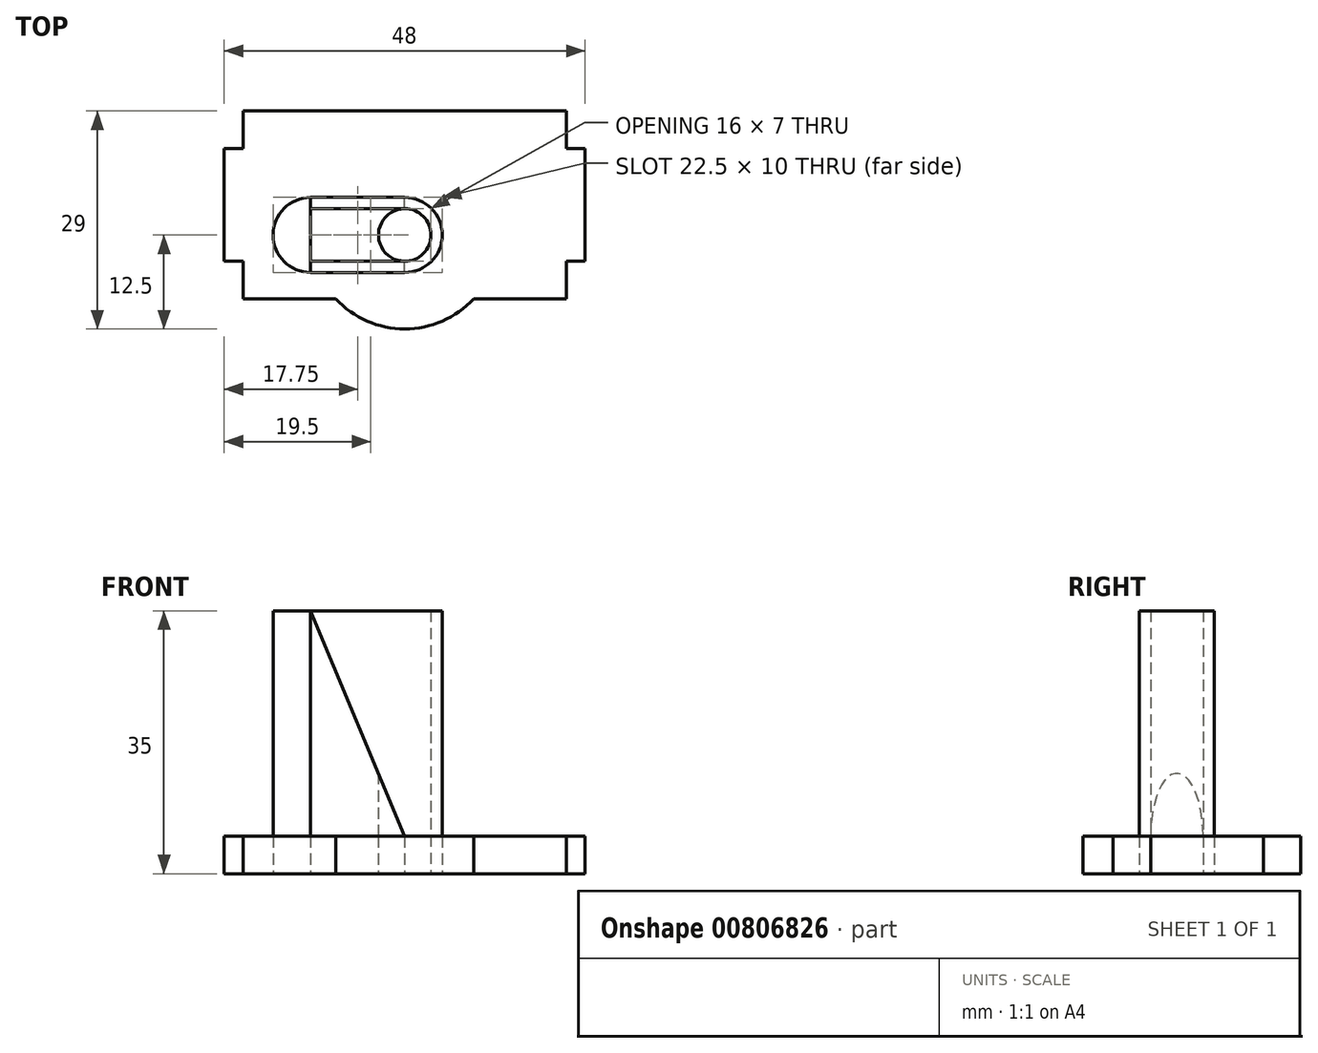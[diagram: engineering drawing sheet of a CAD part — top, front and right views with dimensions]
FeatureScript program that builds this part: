
annotation { "Feature Type Name" : "Feature", "Feature Type Description" : "" }
export const myFeature = defineFeature(function(context is Context, id is Id, definition is map)
    precondition{}
    {
        {
            var Q0;
            Q0=qCreatedBy(makeId("Top.planeOp"),FACE);
            var sketch = newSketch(context, id + "F0", { "sketchPlane" : qUnion([Q0])});
            skCircle(sketch, "E0", {"center": v(0, 0) * mm, "radius": 12.5 * mm});
            skCircle(sketch, "E1", {"center": v(0, 0) * mm, "radius": 3.5 * mm});
            skCircle(sketch, "E2", {"center": v(-12.5, 0) * mm, "radius": 5 * mm});
            skCircle(sketch, "E3", {"center": v(-12.5, 0) * mm, "radius": 3 * mm});
            skCircle(sketch, "E4", {"center": v(0, 0) * mm, "radius": 5 * mm});
            skLineSegment(sketch, "E5.bottom", {"start": v(0, 3.5) * mm, "end": v(-12.5, 3.5) * mm});
            skLineSegment(sketch, "E5.top", {"start": v(0, 5) * mm, "end": v(-12.5, 5) * mm});
            skLineSegment(sketch, "E5.left", {"start": v(0, 3.5) * mm, "end": v(0, 5) * mm});
            skLineSegment(sketch, "E5.right", {"start": v(-12.5, 3.5) * mm, "end": v(-12.5, 5) * mm});
            skLineSegment(sketch, "E6.bottom", {"start": v(0, -3.5) * mm, "end": v(-12.5, -3.5) * mm});
            skLineSegment(sketch, "E6.top", {"start": v(0, -5) * mm, "end": v(-12.5, -5) * mm});
            skLineSegment(sketch, "E6.left", {"start": v(0, -3.5) * mm, "end": v(0, -5) * mm});
            skLineSegment(sketch, "E6.right", {"start": v(-12.5, -3.5) * mm, "end": v(-12.5, -5) * mm});
            skLineSegment(sketch, "E7.bottom", {"start": v(12.5, 5) * mm, "end": v(-12.5, 5) * mm});
            skLineSegment(sketch, "E7.top", {"start": v(12.5, -5) * mm, "end": v(-12.5, -5) * mm});
            skLineSegment(sketch, "E7.right", {"start": v(-12.5, 5) * mm, "end": v(-12.5, -5) * mm});
            skLineSegment(sketch, "E8.bottom", {"start": v(0, 0) * mm, "end": v(24, 0) * mm});
            skLineSegment(sketch, "E8.top", {"start": v(0, -8.5) * mm, "end": v(24, -8.5) * mm});
            skLineSegment(sketch, "E8.left", {"start": v(0, 0) * mm, "end": v(0, -8.5) * mm});
            skLineSegment(sketch, "E8.right", {"start": v(24, 0) * mm, "end": v(24, -8.5) * mm});
            skLineSegment(sketch, "E9.bottom", {"start": v(0, 0) * mm, "end": v(-24, 0) * mm});
            skLineSegment(sketch, "E9.top", {"start": v(0, -8.5) * mm, "end": v(-24, -8.5) * mm});
            skLineSegment(sketch, "E9.right", {"start": v(-24, 0) * mm, "end": v(-24, -8.5) * mm});
            skLineSegment(sketch, "E10.top", {"start": v(0, 16.5) * mm, "end": v(24, 16.5) * mm});
            skLineSegment(sketch, "E10.left", {"start": v(0, 0) * mm, "end": v(0, 16.5) * mm});
            skLineSegment(sketch, "E10.right", {"start": v(24, 0) * mm, "end": v(24, 16.5) * mm});
            skLineSegment(sketch, "E11.top", {"start": v(0, 16.5) * mm, "end": v(-24, 16.5) * mm});
            skLineSegment(sketch, "E11.right", {"start": v(-24, 0) * mm, "end": v(-24, 16.5) * mm});
            skLineSegment(sketch, "E12.bottom", {"start": v(-24, -8.5) * mm, "end": v(-21.5, -8.5) * mm});
            skLineSegment(sketch, "E12.top", {"start": v(-24, -3.5) * mm, "end": v(-21.5, -3.5) * mm});
            skLineSegment(sketch, "E12.left", {"start": v(-24, -8.5) * mm, "end": v(-24, -3.5) * mm});
            skLineSegment(sketch, "E12.right", {"start": v(-21.5, -8.5) * mm, "end": v(-21.5, -3.5) * mm});
            skLineSegment(sketch, "E13.bottom", {"start": v(-24, 16.5) * mm, "end": v(-21.5, 16.5) * mm});
            skLineSegment(sketch, "E13.top", {"start": v(-24, 11.5) * mm, "end": v(-21.5, 11.5) * mm});
            skLineSegment(sketch, "E13.left", {"start": v(-24, 16.5) * mm, "end": v(-24, 11.5) * mm});
            skLineSegment(sketch, "E13.right", {"start": v(-21.5, 16.5) * mm, "end": v(-21.5, 11.5) * mm});
            skLineSegment(sketch, "E14.bottom", {"start": v(24, 16.5) * mm, "end": v(21.5, 16.5) * mm});
            skLineSegment(sketch, "E14.top", {"start": v(24, 11.5) * mm, "end": v(21.5, 11.5) * mm});
            skLineSegment(sketch, "E14.left", {"start": v(24, 16.5) * mm, "end": v(24, 11.5) * mm});
            skLineSegment(sketch, "E14.right", {"start": v(21.5, 16.5) * mm, "end": v(21.5, 11.5) * mm});
            skPoint(sketch, "E15.oppositeSnap0", {"position": v(-6.25, -3.5) * mm});
            skLineSegment(sketch, "E15.bottom", {"start": v(24, -8.5) * mm, "end": v(21.5, -8.5) * mm});
            skLineSegment(sketch, "E15.top", {"start": v(24, -3.5) * mm, "end": v(21.5, -3.5) * mm});
            skLineSegment(sketch, "E15.left", {"start": v(24, -8.5) * mm, "end": v(24, -3.5) * mm});
            skLineSegment(sketch, "E15.right", {"start": v(21.5, -8.5) * mm, "end": v(21.5, -3.5) * mm});
            skSolve(sketch);
        }
        {
            var Q0;
            Q0=qCreatedBy(makeId("Front.planeOp"),FACE);
            var sketch = newSketch(context, id + "F1", { "sketchPlane" : qUnion([Q0])});
            skLineSegment(sketch, "E16", {"start": v(0, 0) * mm, "end": v(0, 10) * mm});
            skLineSegment(sketch, "E17", {"start": v(0, 10) * mm, "end": v(-12.5, 10) * mm});
            skLineSegment(sketch, "E18", {"start": v(-12.5, 10) * mm, "end": v(-12.5, 40) * mm});
            skLineSegment(sketch, "E19", {"start": v(-12.5, 40) * mm, "end": v(0, 10) * mm});
            skSolve(sketch);
        }
        {
            var Q0;
            Q0=makeQuery(id+"F1.imprint","IMPRINT",FACE,{"disambiguationData":[TD([[makeQuery(id+"F1.imprint","IMPRINT",EDGE,{"derivedFrom":sQuery(id+"F1.wireOp",EDGE,"E17")}),-1.0]])]});
            extrude(context, id + "F2", {"entities" : qUnion([Q0]), "endBound" : BoundingType.SYMMETRIC, "depth" : 10 * mm, "offsetDistance" : 25 * mm});
        }
        {
            var Q0;
            {var subQ1=sQuery(id+"F0.wireOp",EDGE,"E5.left");Q0=makeQuery(id+"F0.imprint","IMPRINT",FACE,{"disambiguationData":[TD([[makeQuery(id+"F0.imprint","IMPRINT",EDGE,{"derivedFrom":subQ1}),-1.0]])]});}
            var Q1;
            {var subQ1=sQuery(id+"F0.wireOp",EDGE,"E6.left");Q1=makeQuery(id+"F0.imprint","IMPRINT",FACE,{"disambiguationData":[TD([[makeQuery(id+"F0.imprint","IMPRINT",EDGE,{"derivedFrom":subQ1}),1.0]])]});}
            var Q2;
            {var subQ3=sQuery(id+"F0.wireOp",EDGE,"E2");var subQ5=sQuery(id+"F0.wireOp",EDGE,"E0");var subQ6=makeQuery(id+"F0.imprint","INTERSECT",VERTEX,{"disambiguationData":[OD(1.0)],"derivedFrom":[subQ5,subQ3]});Q2=makeQuery(id+"F0.imprint","IMPRINT",FACE,{"disambiguationData":[TD([[makeQuery(id+"F0.imprint","IMPRINT",EDGE,{"disambiguationData":[TD([[subQ6,-1.0]])],"derivedFrom":subQ5}),1.0]])]});}
            var Q3;
            {var subQ5=sQuery(id+"F0.wireOp",EDGE,"E5.top");var subQ7=sQuery(id+"F0.wireOp",EDGE,"E0");var subQ9=makeQuery(id+"F0.imprint","INTERSECT",VERTEX,{"derivedFrom":[subQ7,subQ5]});Q3=makeQuery(id+"F0.imprint","IMPRINT",FACE,{"disambiguationData":[TD([[makeQuery(id+"F0.imprint","IMPRINT",EDGE,{"disambiguationData":[TD([[subQ9,-1.0]])],"derivedFrom":subQ7}),1.0]])]});}
            var Q4;
            {var subQ4=sQuery(id+"F0.wireOp",EDGE,"E5.left");Q4=makeQuery(id+"F0.imprint","IMPRINT",FACE,{"disambiguationData":[TD([[makeQuery(id+"F0.imprint","IMPRINT",EDGE,{"derivedFrom":subQ4}),1.0]])]});}
            var Q5;
            {var subQ4=sQuery(id+"F0.wireOp",EDGE,"E6.left");Q5=makeQuery(id+"F0.imprint","IMPRINT",FACE,{"disambiguationData":[TD([[makeQuery(id+"F0.imprint","IMPRINT",EDGE,{"derivedFrom":subQ4}),-1.0]])]});}
            var Q6;
            {var subQ1=sQuery(id+"F0.wireOp",EDGE,"E5.right");Q6=makeQuery(id+"F0.imprint","IMPRINT",FACE,{"disambiguationData":[TD([[makeQuery(id+"F0.imprint","IMPRINT",EDGE,{"derivedFrom":subQ1}),1.0]])]});}
            var Q7;
            {var subQ1=sQuery(id+"F0.wireOp",EDGE,"E6.right");Q7=makeQuery(id+"F0.imprint","IMPRINT",FACE,{"disambiguationData":[TD([[makeQuery(id+"F0.imprint","IMPRINT",EDGE,{"derivedFrom":subQ1}),-1.0]])]});}
            var Q8;
            {var subQ0=sQuery(id+"F0.wireOp",EDGE,"E9.bottom");var subQ1=sQuery(id+"F0.wireOp",EDGE,"E3");var subQ2=makeQuery(id+"F0.imprint","INTERSECT",VERTEX,{"disambiguationData":[OD(1.0)],"derivedFrom":[subQ1,subQ0]});Q8=makeQuery(id+"F0.imprint","IMPRINT",FACE,{"disambiguationData":[TD([[makeQuery(id+"F0.imprint","IMPRINT",EDGE,{"disambiguationData":[TD([[subQ2,-1.0]])],"derivedFrom":subQ1}),1.0]])]});}
            var Q9;
            {var subQ0=sQuery(id+"F0.wireOp",EDGE,"E7.right");var subQ1=sQuery(id+"F0.wireOp",EDGE,"E3");var subQ2=makeQuery(id+"F0.imprint","INTERSECT",VERTEX,{"disambiguationData":[OD(0.0)],"derivedFrom":[subQ1,subQ0]});Q9=makeQuery(id+"F0.imprint","IMPRINT",FACE,{"disambiguationData":[TD([[makeQuery(id+"F0.imprint","IMPRINT",EDGE,{"disambiguationData":[TD([[subQ2,-1.0]])],"derivedFrom":subQ1}),1.0]])]});}
            var Q10;
            {var subQ5=sQuery(id+"F0.wireOp",EDGE,"E5.right");Q10=makeQuery(id+"F0.imprint","IMPRINT",FACE,{"disambiguationData":[TD([[makeQuery(id+"F0.imprint","IMPRINT",EDGE,{"derivedFrom":subQ5}),-1.0]])]});}
            var Q11;
            {var subQ5=sQuery(id+"F0.wireOp",EDGE,"E6.right");Q11=makeQuery(id+"F0.imprint","IMPRINT",FACE,{"disambiguationData":[TD([[makeQuery(id+"F0.imprint","IMPRINT",EDGE,{"derivedFrom":subQ5}),1.0]])]});}
            var Q12;
            {var subQ0=sQuery(id+"F0.wireOp",EDGE,"E2");var subQ1=sQuery(id+"F0.wireOp",EDGE,"E0");var subQ2=makeQuery(id+"F0.imprint","INTERSECT",VERTEX,{"disambiguationData":[OD(0.0)],"derivedFrom":[subQ1,subQ0]});Q12=makeQuery(id+"F0.imprint","IMPRINT",FACE,{"disambiguationData":[TD([[makeQuery(id+"F0.imprint","IMPRINT",EDGE,{"disambiguationData":[TD([[subQ2,-1.0]])],"derivedFrom":subQ1}),1.0]])]});}
            var Q13;
            {var subQ0=sQuery(id+"F0.wireOp",EDGE,"E6.bottom");var subQ1=sQuery(id+"F0.wireOp",EDGE,"E0");var subQ2=makeQuery(id+"F0.imprint","INTERSECT",VERTEX,{"derivedFrom":[subQ1,subQ0]});Q13=makeQuery(id+"F0.imprint","IMPRINT",FACE,{"disambiguationData":[TD([[makeQuery(id+"F0.imprint","IMPRINT",EDGE,{"disambiguationData":[TD([[subQ2,-1.0]])],"derivedFrom":subQ1}),1.0]])]});}
            var Q14;
            {var subQ0=sQuery(id+"F0.wireOp",EDGE,"E5.top");var subQ1=sQuery(id+"F0.wireOp",EDGE,"E0");var subQ2=makeQuery(id+"F0.imprint","INTERSECT",VERTEX,{"derivedFrom":[subQ1,subQ0]});Q14=makeQuery(id+"F0.imprint","IMPRINT",FACE,{"disambiguationData":[TD([[makeQuery(id+"F0.imprint","IMPRINT",EDGE,{"disambiguationData":[TD([[subQ2,-1.0]])],"derivedFrom":subQ1}),-1.0]])]});}
            var Q15;
            {var subQ0=sQuery(id+"F0.wireOp",EDGE,"E2");var subQ1=sQuery(id+"F0.wireOp",EDGE,"E0");var subQ2=makeQuery(id+"F0.imprint","INTERSECT",VERTEX,{"disambiguationData":[OD(1.0)],"derivedFrom":[subQ1,subQ0]});Q15=makeQuery(id+"F0.imprint","IMPRINT",FACE,{"disambiguationData":[TD([[makeQuery(id+"F0.imprint","IMPRINT",EDGE,{"disambiguationData":[TD([[subQ2,-1.0]])],"derivedFrom":subQ1}),-1.0]])]});}
            extrude(context, id + "F3", {"entities" : qUnion([Q0, Q1, Q2, Q3, Q4, Q5, Q6, Q7, Q8, Q9, Q10, Q11, Q12, Q13, Q14, Q15]), "depth" : 40 * mm, "offsetDistance" : 25 * mm});
        }
        {
            var Q0;
            {var subQ14=sQuery(id+"F0.wireOp",EDGE,"E13.top");Q0=makeQuery(id+"F0.imprint","IMPRINT",FACE,{"disambiguationData":[TD([[makeQuery(id+"F0.imprint","IMPRINT",EDGE,{"derivedFrom":subQ14}),-1.0]])]});}
            var Q1;
            {var subQ9=sQuery(id+"F0.wireOp",EDGE,"E12.top");Q1=makeQuery(id+"F0.imprint","IMPRINT",FACE,{"disambiguationData":[TD([[makeQuery(id+"F0.imprint","IMPRINT",EDGE,{"derivedFrom":subQ9}),1.0]])]});}
            var Q2;
            {var subQ0=sQuery(id+"F0.wireOp",EDGE,"E9.top");var subQ1=sQuery(id+"F0.wireOp",EDGE,"E0");var subQ2=makeQuery(id+"F0.imprint","INTERSECT",VERTEX,{"derivedFrom":[subQ1,subQ0]});Q2=makeQuery(id+"F0.imprint","IMPRINT",FACE,{"disambiguationData":[TD([[makeQuery(id+"F0.imprint","IMPRINT",EDGE,{"disambiguationData":[TD([[subQ2,1.0]])],"derivedFrom":subQ1}),1.0]])]});}
            var Q3;
            {var subQ0=sQuery(id+"F0.wireOp",EDGE,"E7.top");var subQ1=sQuery(id+"F0.wireOp",EDGE,"E0");var subQ2=makeQuery(id+"F0.imprint","INTERSECT",VERTEX,{"derivedFrom":[subQ1,subQ0]});Q3=makeQuery(id+"F0.imprint","IMPRINT",FACE,{"disambiguationData":[TD([[makeQuery(id+"F0.imprint","IMPRINT",EDGE,{"disambiguationData":[TD([[subQ2,1.0]])],"derivedFrom":subQ1}),1.0]])]});}
            var Q4;
            {var subQ0=sQuery(id+"F0.wireOp",EDGE,"E8.top");var subQ1=sQuery(id+"F0.wireOp",EDGE,"E0");var subQ2=makeQuery(id+"F0.imprint","INTERSECT",VERTEX,{"derivedFrom":[subQ1,subQ0]});Q4=makeQuery(id+"F0.imprint","IMPRINT",FACE,{"disambiguationData":[TD([[makeQuery(id+"F0.imprint","IMPRINT",EDGE,{"disambiguationData":[TD([[subQ2,1.0]])],"derivedFrom":subQ1}),1.0]])]});}
            var Q5;
            {var subQ9=sQuery(id+"F0.wireOp",EDGE,"E15.top");Q5=makeQuery(id+"F0.imprint","IMPRINT",FACE,{"disambiguationData":[TD([[makeQuery(id+"F0.imprint","IMPRINT",EDGE,{"derivedFrom":subQ9}),-1.0]])]});}
            var Q6;
            {var subQ8=sQuery(id+"F0.wireOp",EDGE,"E14.top");Q6=makeQuery(id+"F0.imprint","IMPRINT",FACE,{"disambiguationData":[TD([[makeQuery(id+"F0.imprint","IMPRINT",EDGE,{"derivedFrom":subQ8}),1.0]])]});}
            var Q7;
            {var subQ0=sQuery(id+"F0.wireOp",EDGE,"E7.bottom");var subQ1=sQuery(id+"F0.wireOp",EDGE,"E0");var subQ2=makeQuery(id+"F0.imprint","INTERSECT",VERTEX,{"derivedFrom":[subQ1,subQ0]});Q7=makeQuery(id+"F0.imprint","IMPRINT",FACE,{"disambiguationData":[TD([[makeQuery(id+"F0.imprint","IMPRINT",EDGE,{"disambiguationData":[TD([[subQ2,-1.0]])],"derivedFrom":subQ1}),1.0]])]});}
            var Q8;
            {var subQ0=sQuery(id+"F0.wireOp",EDGE,"E10.left");var subQ1=sQuery(id+"F0.wireOp",EDGE,"E0");var subQ2=makeQuery(id+"F0.imprint","INTERSECT",VERTEX,{"derivedFrom":[subQ1,subQ0]});Q8=makeQuery(id+"F0.imprint","IMPRINT",FACE,{"disambiguationData":[TD([[makeQuery(id+"F0.imprint","IMPRINT",EDGE,{"disambiguationData":[TD([[subQ2,-1.0]])],"derivedFrom":subQ1}),1.0]])]});}
            var Q9;
            {var subQ0=sQuery(id+"F0.wireOp",EDGE,"E5.bottom");var subQ5=sQuery(id+"F0.wireOp",EDGE,"E4");var subQ6=makeQuery(id+"F0.imprint","INTERSECT",VERTEX,{"derivedFrom":[subQ5,subQ0]});Q9=makeQuery(id+"F0.imprint","IMPRINT",FACE,{"disambiguationData":[TD([[makeQuery(id+"F0.imprint","IMPRINT",EDGE,{"disambiguationData":[TD([[subQ6,-1.0]])],"derivedFrom":subQ5}),1.0]])]});}
            var Q10;
            {var subQ0=sQuery(id+"F0.wireOp",EDGE,"E5.bottom");var subQ1=sQuery(id+"F0.wireOp",EDGE,"E2");var subQ2=makeQuery(id+"F0.imprint","INTERSECT",VERTEX,{"derivedFrom":[subQ1,subQ0]});Q10=makeQuery(id+"F0.imprint","IMPRINT",FACE,{"disambiguationData":[TD([[makeQuery(id+"F0.imprint","IMPRINT",EDGE,{"disambiguationData":[TD([[subQ2,1.0]])],"derivedFrom":subQ1}),-1.0]])]});}
            var Q11;
            {var subQ0=sQuery(id+"F0.wireOp",EDGE,"E9.bottom");var subQ1=sQuery(id+"F0.wireOp",EDGE,"E2");var subQ2=makeQuery(id+"F0.imprint","INTERSECT",VERTEX,{"disambiguationData":[OD(1.0)],"derivedFrom":[subQ1,subQ0]});Q11=makeQuery(id+"F0.imprint","IMPRINT",FACE,{"disambiguationData":[TD([[makeQuery(id+"F0.imprint","IMPRINT",EDGE,{"disambiguationData":[TD([[subQ2,1.0]])],"derivedFrom":subQ1}),-1.0]])]});}
            var Q12;
            {var subQ0=sQuery(id+"F0.wireOp",EDGE,"E6.bottom");var subQ5=sQuery(id+"F0.wireOp",EDGE,"E4");var subQ6=makeQuery(id+"F0.imprint","INTERSECT",VERTEX,{"derivedFrom":[subQ5,subQ0]});Q12=makeQuery(id+"F0.imprint","IMPRINT",FACE,{"disambiguationData":[TD([[makeQuery(id+"F0.imprint","IMPRINT",EDGE,{"disambiguationData":[TD([[subQ6,1.0]])],"derivedFrom":subQ5}),1.0]])]});}
            var Q13;
            {var subQ1=sQuery(id+"F0.wireOp",EDGE,"E0");var subQ5=sQuery(id+"F0.wireOp",EDGE,"E3");var subQ6=makeQuery(id+"F0.imprint","INTERSECT",VERTEX,{"disambiguationData":[OD(1.0)],"derivedFrom":[subQ1,subQ5]});Q13=makeQuery(id+"F0.imprint","IMPRINT",FACE,{"disambiguationData":[TD([[makeQuery(id+"F0.imprint","IMPRINT",EDGE,{"disambiguationData":[TD([[subQ6,-1.0]])],"derivedFrom":subQ1}),1.0]])]});}
            var Q14;
            {var subQ0=sQuery(id+"F0.wireOp",EDGE,"E5.bottom");var subQ1=sQuery(id+"F0.wireOp",EDGE,"E0");var subQ2=makeQuery(id+"F0.imprint","INTERSECT",VERTEX,{"derivedFrom":[subQ1,subQ0]});Q14=makeQuery(id+"F0.imprint","IMPRINT",FACE,{"disambiguationData":[TD([[makeQuery(id+"F0.imprint","IMPRINT",EDGE,{"disambiguationData":[TD([[subQ2,-1.0]])],"derivedFrom":subQ1}),1.0]])]});}
            var Q15;
            {var subQ1=sQuery(id+"F0.wireOp",EDGE,"E0");var subQ3=sQuery(id+"F0.wireOp",EDGE,"E3");var subQ4=makeQuery(id+"F0.imprint","INTERSECT",VERTEX,{"disambiguationData":[OD(0.0)],"derivedFrom":[subQ1,subQ3]});Q15=makeQuery(id+"F0.imprint","IMPRINT",FACE,{"disambiguationData":[TD([[makeQuery(id+"F0.imprint","IMPRINT",EDGE,{"disambiguationData":[TD([[subQ4,1.0]])],"derivedFrom":subQ3}),1.0]])]});}
            var Q16;
            {var subQ1=sQuery(id+"F0.wireOp",EDGE,"E0");var subQ3=sQuery(id+"F0.wireOp",EDGE,"E3");var subQ4=makeQuery(id+"F0.imprint","INTERSECT",VERTEX,{"disambiguationData":[OD(1.0)],"derivedFrom":[subQ1,subQ3]});Q16=makeQuery(id+"F0.imprint","IMPRINT",FACE,{"disambiguationData":[TD([[makeQuery(id+"F0.imprint","IMPRINT",EDGE,{"disambiguationData":[TD([[subQ4,-1.0]])],"derivedFrom":subQ3}),1.0]])]});}
            var Q17;
            {var subQ1=sQuery(id+"F0.wireOp",EDGE,"E0");var subQ3=sQuery(id+"F0.wireOp",EDGE,"E3");var subQ4=makeQuery(id+"F0.imprint","INTERSECT",VERTEX,{"disambiguationData":[OD(1.0)],"derivedFrom":[subQ1,subQ3]});Q17=makeQuery(id+"F0.imprint","IMPRINT",FACE,{"disambiguationData":[TD([[makeQuery(id+"F0.imprint","IMPRINT",EDGE,{"disambiguationData":[TD([[subQ4,1.0]])],"derivedFrom":subQ3}),1.0]])]});}
            var Q18;
            {var subQ0=sQuery(id+"F0.wireOp",EDGE,"E7.right");var subQ3=sQuery(id+"F0.wireOp",EDGE,"E3");var subQ5=makeQuery(id+"F0.imprint","INTERSECT",VERTEX,{"disambiguationData":[OD(0.0)],"derivedFrom":[subQ3,subQ0]});Q18=makeQuery(id+"F0.imprint","IMPRINT",FACE,{"disambiguationData":[TD([[makeQuery(id+"F0.imprint","IMPRINT",EDGE,{"disambiguationData":[TD([[subQ5,1.0]])],"derivedFrom":subQ3}),1.0]])]});}
            var Q19;
            {var subQ0=sQuery(id+"F0.wireOp",EDGE,"E5.bottom");var subQ1=sQuery(id+"F0.wireOp",EDGE,"E0");var subQ2=makeQuery(id+"F0.imprint","INTERSECT",VERTEX,{"derivedFrom":[subQ1,subQ0]});Q19=makeQuery(id+"F0.imprint","IMPRINT",FACE,{"disambiguationData":[TD([[makeQuery(id+"F0.imprint","IMPRINT",EDGE,{"disambiguationData":[TD([[subQ2,-1.0]])],"derivedFrom":subQ1}),-1.0]])]});}
            var Q20;
            {var subQ0=sQuery(id+"F0.wireOp",EDGE,"E3");var subQ1=sQuery(id+"F0.wireOp",EDGE,"E0");var subQ2=makeQuery(id+"F0.imprint","INTERSECT",VERTEX,{"disambiguationData":[OD(1.0)],"derivedFrom":[subQ1,subQ0]});Q20=makeQuery(id+"F0.imprint","IMPRINT",FACE,{"disambiguationData":[TD([[makeQuery(id+"F0.imprint","IMPRINT",EDGE,{"disambiguationData":[TD([[subQ2,-1.0]])],"derivedFrom":subQ1}),-1.0]])]});}
            var Q21;
            {var subQ0=sQuery(id+"F0.wireOp",EDGE,"E7.bottom");var subQ1=sQuery(id+"F0.wireOp",EDGE,"E0");var subQ2=makeQuery(id+"F0.imprint","INTERSECT",VERTEX,{"derivedFrom":[subQ1,subQ0]});Q21=makeQuery(id+"F0.imprint","IMPRINT",FACE,{"disambiguationData":[TD([[makeQuery(id+"F0.imprint","IMPRINT",EDGE,{"disambiguationData":[TD([[subQ2,1.0]])],"derivedFrom":subQ1}),1.0]])]});}
            var Q22;
            {var subQ0=sQuery(id+"F0.wireOp",EDGE,"E7.top");var subQ1=sQuery(id+"F0.wireOp",EDGE,"E0");var subQ2=makeQuery(id+"F0.imprint","INTERSECT",VERTEX,{"derivedFrom":[subQ1,subQ0]});Q22=makeQuery(id+"F0.imprint","IMPRINT",FACE,{"disambiguationData":[TD([[makeQuery(id+"F0.imprint","IMPRINT",EDGE,{"disambiguationData":[TD([[subQ2,-1.0]])],"derivedFrom":subQ1}),1.0]])]});}
            extrude(context, id + "F4", {"entities" : qUnion([Q0, Q1, Q2, Q3, Q4, Q5, Q6, Q7, Q8, Q9, Q10, Q11, Q12, Q13, Q14, Q15, Q16, Q17, Q18, Q19, Q20, Q21, Q22]), "depth" : 10 * mm, "offsetDistance" : 25 * mm});
        }
        {
            var Q0;
            {var subQ1=sQuery(id+"F0.wireOp",EDGE,"E1");var subQ3=sQuery(id+"F0.wireOp",EDGE,"E9.bottom");var subQ4=makeQuery(id+"F0.imprint","INTERSECT",VERTEX,{"derivedFrom":[subQ1,subQ3]});Q0=makeQuery(id+"F0.imprint","IMPRINT",FACE,{"disambiguationData":[TD([[makeQuery(id+"F0.imprint","IMPRINT",EDGE,{"disambiguationData":[TD([[subQ4,1.0]])],"derivedFrom":subQ1}),1.0]])]});}
            var Q1;
            {var subQ1=sQuery(id+"F0.wireOp",EDGE,"E1");var subQ3=sQuery(id+"F0.wireOp",EDGE,"E9.bottom");var subQ4=makeQuery(id+"F0.imprint","INTERSECT",VERTEX,{"derivedFrom":[subQ1,subQ3]});Q1=makeQuery(id+"F0.imprint","IMPRINT",FACE,{"disambiguationData":[TD([[makeQuery(id+"F0.imprint","IMPRINT",EDGE,{"disambiguationData":[TD([[subQ4,-1.0]])],"derivedFrom":subQ1}),1.0]])]});}
            extrude(context, id + "F5", {"entities" : qUnion([Q0, Q1]), "operationType" : NewBodyOperationType.REMOVE, "oppositeDirection" : true, "depth" : -40 * mm, "offsetDistance" : 25 * mm});
        }
        {
            var Q0;
            Q0=qCreatedBy(makeId("Front.planeOp"),FACE);
            var sketch = newSketch(context, id + "F6", { "sketchPlane" : qUnion([Q0])});
            skLineSegment(sketch, "E20", {"start": v(0, 0) * mm, "end": v(0, 25) * mm});
            skLineSegment(sketch, "E21.bottom", {"start": v(-25, 45) * mm, "end": v(25, 45) * mm});
            skLineSegment(sketch, "E21.top", {"start": v(-25, 5) * mm, "end": v(25, 5) * mm});
            skLineSegment(sketch, "E21.left", {"start": v(-25, 45) * mm, "end": v(-25, 5) * mm});
            skLineSegment(sketch, "E21.right", {"start": v(25, 45) * mm, "end": v(25, 5) * mm});
            skPoint(sketch, "E21.middle", {"position": v(0, 25) * mm});
            skSolve(sketch);
        }
        {
            var Q0;
            Q0=qSketchRegion(id+"F6",true);
            extrude(context, id + "F7", {"entities" : qUnion([Q0]), "operationType" : NewBodyOperationType.INTERSECT, "endBound" : BoundingType.SYMMETRIC, "depth" : 40 * mm, "offsetDistance" : 25 * mm});
        }
    });
